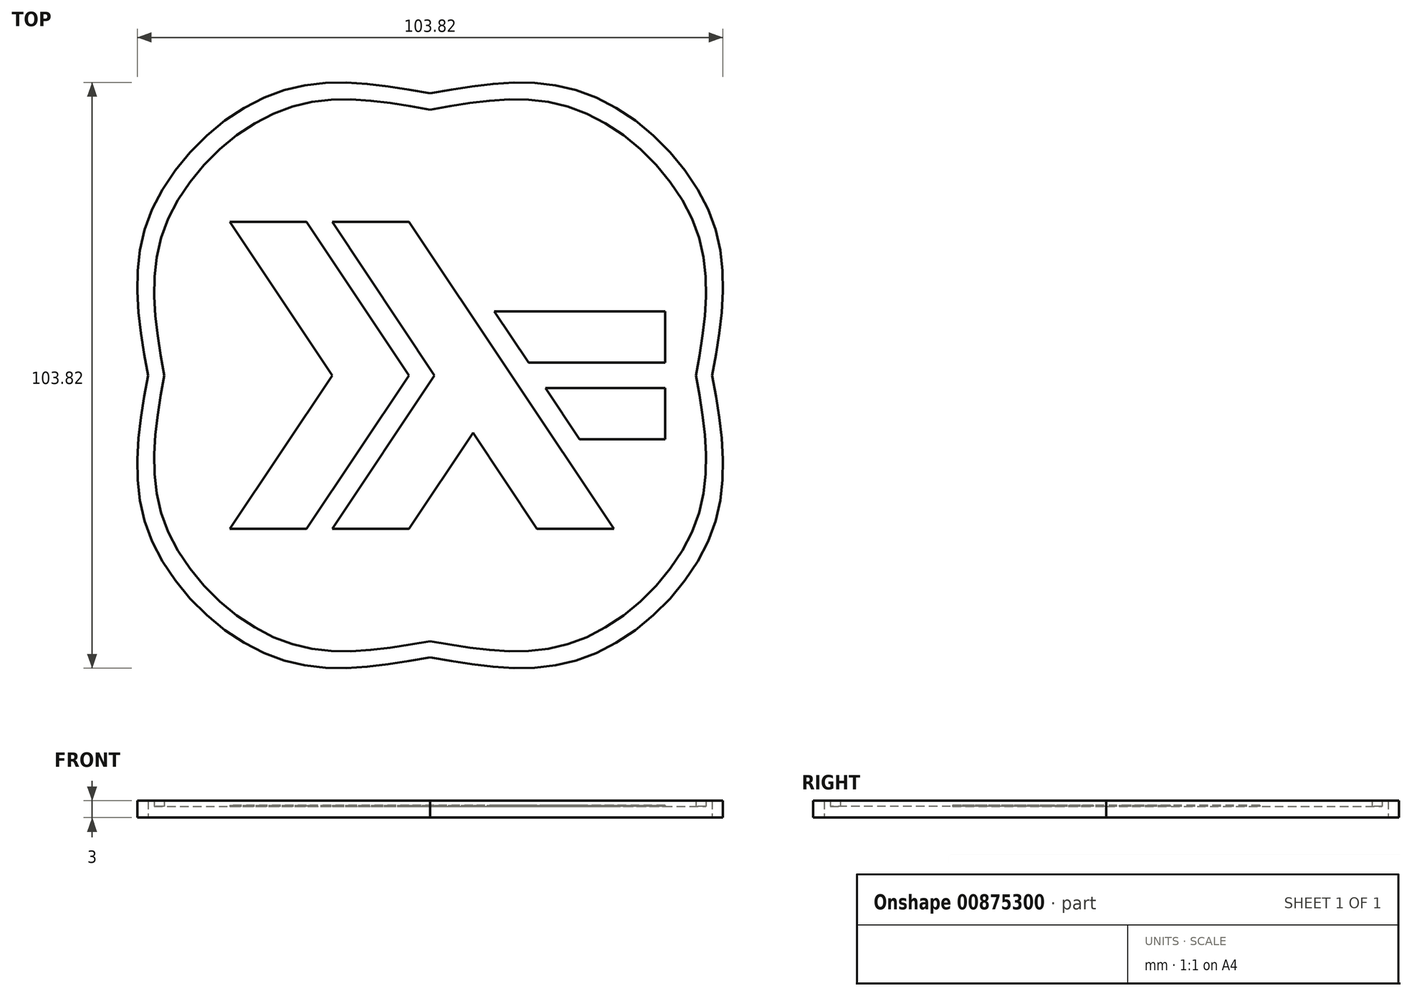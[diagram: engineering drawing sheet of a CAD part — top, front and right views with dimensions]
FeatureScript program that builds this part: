
annotation { "Feature Type Name" : "Feature", "Feature Type Description" : "" }
export const myFeature = defineFeature(function(context is Context, id is Id, definition is map)
    precondition{}
    {
        {
            var Q0;
            Q0=qCreatedBy(makeId("Top.planeOp"),FACE);
            var sketch = newSketch(context, id + "F0", { "sketchPlane" : qUnion([Q0])});
            skLineSegment(sketch, "E0", {"start": v(-35.52, -27.23) * mm, "end": v(-17.36, 0) * mm});
            skLineSegment(sketch, "E1", {"start": v(-17.36, 0) * mm, "end": v(-35.52, 27.23) * mm});
            skLineSegment(sketch, "E2", {"start": v(-35.52, 27.23) * mm, "end": v(-21.9, 27.23) * mm});
            skLineSegment(sketch, "E3", {"start": v(-21.9, 27.23) * mm, "end": v(-3.75, 0) * mm});
            skLineSegment(sketch, "E4", {"start": v(-3.75, 0) * mm, "end": v(-21.9, -27.23) * mm});
            skLineSegment(sketch, "E5", {"start": v(-21.9, -27.23) * mm, "end": v(-35.52, -27.23) * mm});
            skLineSegment(sketch, "E6", {"start": v(-17.36, -27.23) * mm, "end": v(0.79, 0) * mm});
            skLineSegment(sketch, "E7", {"start": v(0.79, 0) * mm, "end": v(-17.36, 27.23) * mm});
            skLineSegment(sketch, "E8", {"start": v(-17.36, 27.23) * mm, "end": v(-3.75, 27.23) * mm});
            skLineSegment(sketch, "E9", {"start": v(-3.75, 27.23) * mm, "end": v(32.56, -27.23) * mm});
            skLineSegment(sketch, "E10", {"start": v(32.56, -27.23) * mm, "end": v(18.94, -27.23) * mm});
            skLineSegment(sketch, "E11", {"start": v(18.94, -27.23) * mm, "end": v(7.6, -10.21) * mm});
            skLineSegment(sketch, "E12", {"start": v(7.6, -10.21) * mm, "end": v(-3.75, -27.23) * mm});
            skLineSegment(sketch, "E13", {"start": v(-3.75, -27.23) * mm, "end": v(-17.36, -27.23) * mm});
            skLineSegment(sketch, "E14", {"start": v(26.5, -11.35) * mm, "end": v(20.46, -2.27) * mm});
            skLineSegment(sketch, "E15", {"start": v(20.46, -2.27) * mm, "end": v(41.64, -2.27) * mm});
            skLineSegment(sketch, "E16", {"start": v(41.64, -2.27) * mm, "end": v(41.64, -11.35) * mm});
            skLineSegment(sketch, "E17", {"start": v(41.64, -11.35) * mm, "end": v(26.5, -11.35) * mm});
            skLineSegment(sketch, "E18", {"start": v(26.5, -11.35) * mm, "end": v(26.5, -11.35) * mm});
            skLineSegment(sketch, "E19", {"start": v(17.43, 2.27) * mm, "end": v(11.38, 11.35) * mm});
            skLineSegment(sketch, "E20", {"start": v(11.38, 11.35) * mm, "end": v(41.64, 11.35) * mm});
            skLineSegment(sketch, "E21", {"start": v(41.64, 11.35) * mm, "end": v(41.64, 2.27) * mm});
            skLineSegment(sketch, "E22", {"start": v(41.64, 2.27) * mm, "end": v(17.43, 2.27) * mm});
            skFitSpline(sketch, "E23", {"points": [v(0, 50) * mm, v(-27.6, 50) * mm, v(-50, 27.6) * mm, v(-50, 0) * mm]});
            skFitSpline(sketch, "E24", {"points": [v(-50, 0) * mm, v(-50, -27.6) * mm, v(-27.6, -50) * mm, v(0, -50) * mm]});
            skFitSpline(sketch, "E25", {"points": [v(0, -50) * mm, v(27.6, -50) * mm, v(50, -27.6) * mm, v(50, 0) * mm]});
            skFitSpline(sketch, "E26", {"points": [v(50, 0) * mm, v(50, 27.6) * mm, v(27.6, 50) * mm, v(0, 50) * mm]});
            skFitSpline(sketch, "E27", {"points": [v(0, 47.11) * mm, v(26.04, 47.11) * mm, v(47.11, 26.04) * mm, v(47.11, 0) * mm]});
            skFitSpline(sketch, "E28", {"points": [v(47.11, 0) * mm, v(47.11, -26.04) * mm, v(26.04, -47.11) * mm, v(0, -47.11) * mm]});
            skFitSpline(sketch, "E29", {"points": [v(0, -47.11) * mm, v(-26.04, -47.11) * mm, v(-47.11, -26.04) * mm, v(-47.11, 0) * mm]});
            skFitSpline(sketch, "E30", {"points": [v(-47.11, 0) * mm, v(-47.11, 26.04) * mm, v(-26.04, 47.11) * mm, v(0, 47.11) * mm]});
            skSolve(sketch);
        }
        {
            var Q0;
            Q0=makeQuery(id+"F0.imprint","IMPRINT",FACE,{"disambiguationData":[TD([[makeQuery(id+"F0.imprint","IMPRINT",EDGE,{"derivedFrom":sQuery(id+"F0.wireOp",EDGE,"E6")}),-1.0]])]});
            var Q1;
            Q1=makeQuery(id+"F0.imprint","IMPRINT",FACE,{"disambiguationData":[TD([[makeQuery(id+"F0.imprint","IMPRINT",EDGE,{"derivedFrom":sQuery(id+"F0.wireOp",EDGE,"E0")}),-1.0]])]});
            var Q2;
            Q2=makeQuery(id+"F0.imprint","IMPRINT",FACE,{"disambiguationData":[TD([[makeQuery(id+"F0.imprint","IMPRINT",EDGE,{"derivedFrom":sQuery(id+"F0.wireOp",EDGE,"E19")}),-1.0]])]});
            var Q3;
            Q3=makeQuery(id+"F0.imprint","IMPRINT",FACE,{"disambiguationData":[TD([[makeQuery(id+"F0.imprint","IMPRINT",EDGE,{"derivedFrom":sQuery(id+"F0.wireOp",EDGE,"E14")}),-1.0]])]});
            extrude(context, id + "F1", {"entities" : qUnion([Q0, Q1, Q2, Q3]), "depth" : 2.2 * mm, "offsetDistance" : 25 * mm});
        }
        {
            var Q0;
            Q0=makeQuery(id+"F0.imprint","IMPRINT",FACE,{"disambiguationData":[TD([[makeQuery(id+"F0.imprint","IMPRINT",EDGE,{"derivedFrom":sQuery(id+"F0.wireOp",EDGE,"E23")}),1.0]])]});
            extrude(context, id + "F2", {"entities" : qUnion([Q0]), "depth" : 3 * mm, "offsetDistance" : 25 * mm});
        }
        {
            var Q0;
            Q0=makeQuery(id+"F0.imprint","IMPRINT",FACE,{"disambiguationData":[TD([[makeQuery(id+"F0.imprint","IMPRINT",EDGE,{"derivedFrom":sQuery(id+"F0.wireOp",EDGE,"E0")}),1.0]])]});
            extrude(context, id + "F3", {"entities" : qUnion([Q0]), "operationType" : NewBodyOperationType.ADD, "depth" : 2 * mm, "offsetDistance" : 25 * mm});
        }
    });
